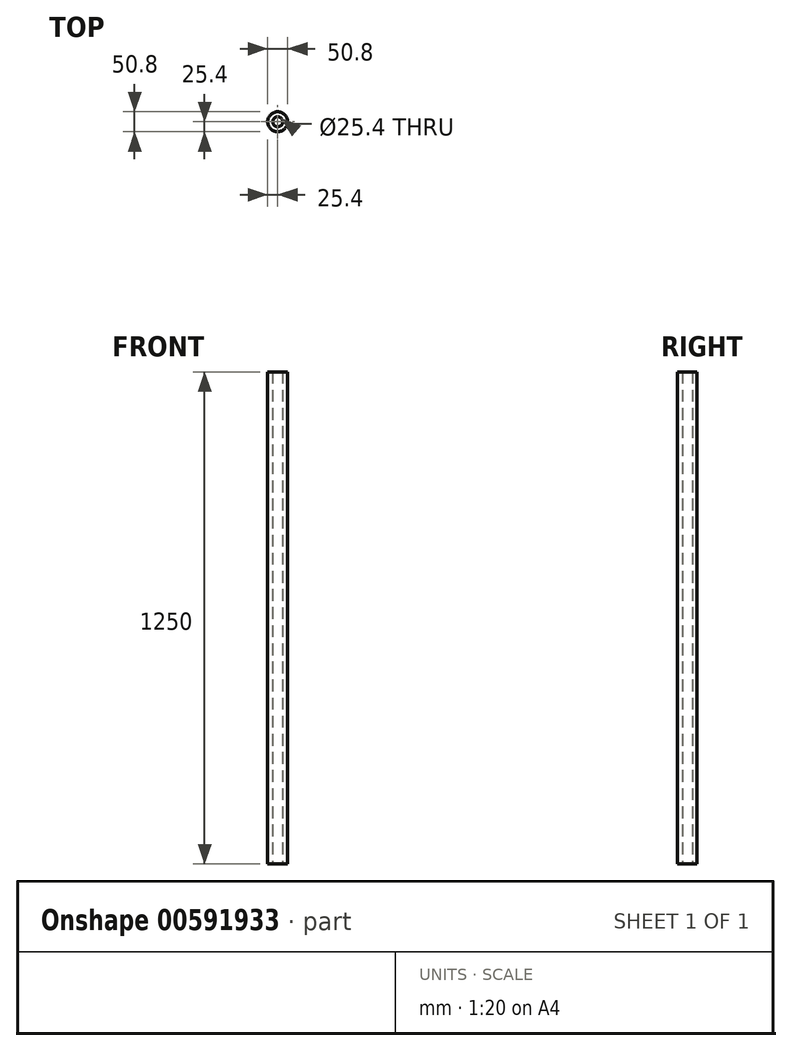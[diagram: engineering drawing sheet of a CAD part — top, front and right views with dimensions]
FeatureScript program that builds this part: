
annotation { "Feature Type Name" : "Feature", "Feature Type Description" : "" }
export const myFeature = defineFeature(function(context is Context, id is Id, definition is map)
    precondition{}
    {
        {
            var Q0;
            Q0=qCreatedBy(makeId("Top.planeOp"),FACE);
            var sketch = newSketch(context, id + "F0", { "sketchPlane" : qUnion([Q0])});
            skCircle(sketch, "E0", {"center": v(0, 0) * mm, "radius": 25.4 * mm});
            skCircle(sketch, "E1", {"center": v(0, 0) * mm, "radius": 12.7 * mm});
            skSolve(sketch);
        }
        {
            var Q0;
            Q0=qSketchRegion(id+"F0",true);
            extrude(context, id + "F1", {"entities" : qUnion([Q0]), "depth" : 1250 * mm, "offsetDistance" : 25.4 * mm});
        }
    });
